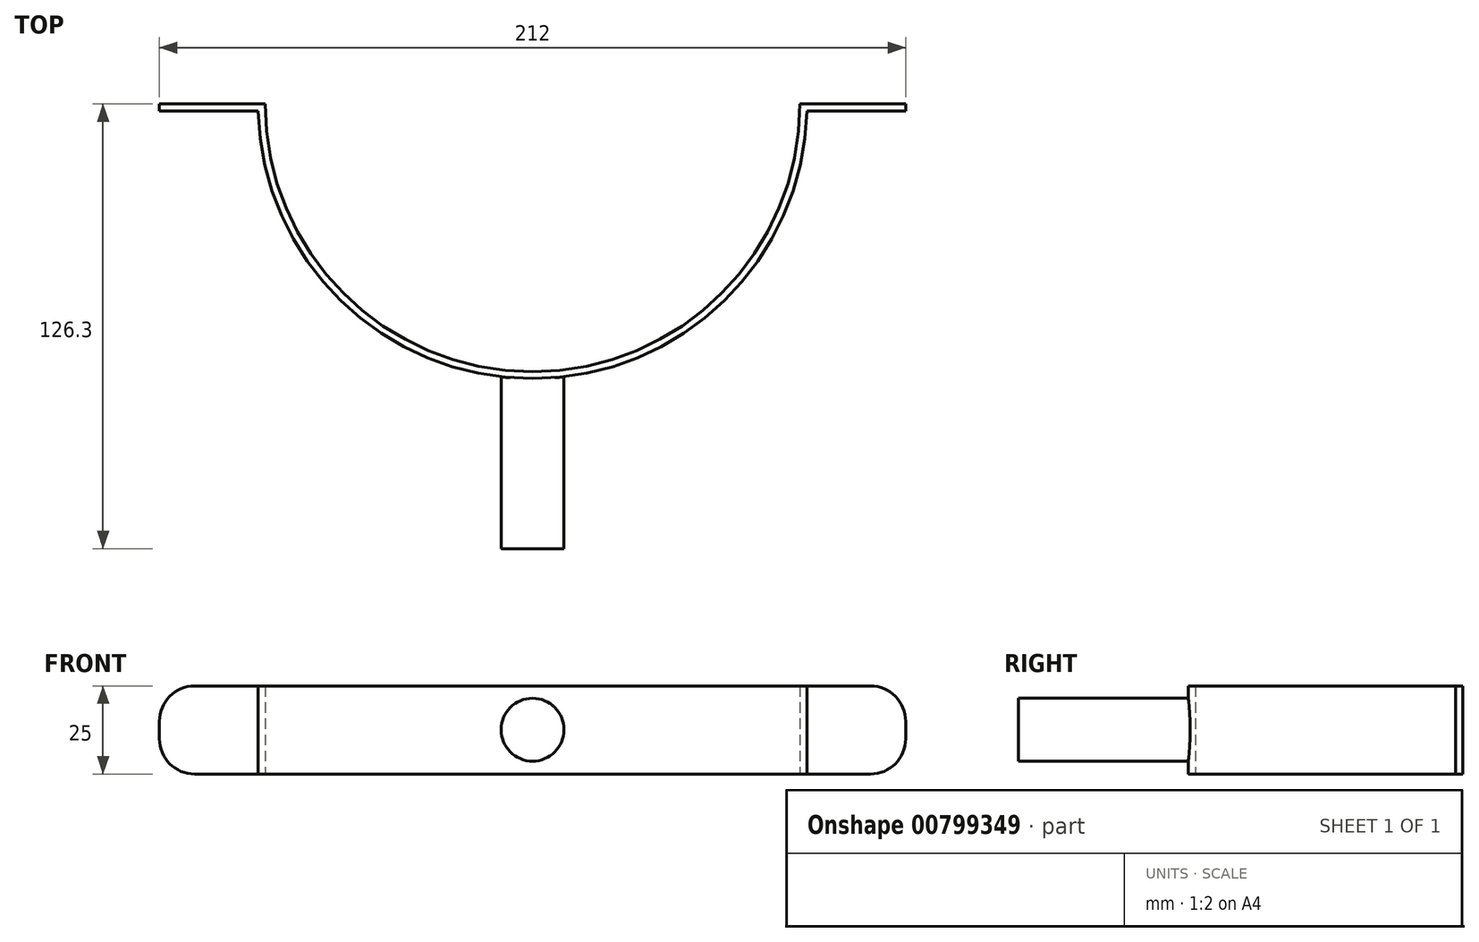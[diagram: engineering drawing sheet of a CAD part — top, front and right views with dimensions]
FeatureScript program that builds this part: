
annotation { "Feature Type Name" : "Feature", "Feature Type Description" : "" }
export const myFeature = defineFeature(function(context is Context, id is Id, definition is map)
    precondition{}
    {
        {
            var Q0;
            Q0=qCreatedBy(makeId("Top.planeOp"),FACE);
            var sketch = newSketch(context, id + "F0", { "sketchPlane" : qUnion([Q0])});
            skArc(sketch, "E0", {"start": v(-76, 0) * mm, "mid": v(0, -76) * mm, "end": v(76, 0) * mm});
            skLineSegment(sketch, "E1", {"start": v(-76, 0) * mm, "end": v(-106, 0) * mm});
            skLineSegment(sketch, "E2", {"start": v(-106, 0) * mm, "end": v(-76, 0) * mm});
            skLineSegment(sketch, "E3", {"start": v(76, 0) * mm, "end": v(106, 0) * mm});
            skArc(sketch, "E4", {"start": v(-77.97, -2) * mm, "mid": v(0, -78) * mm, "end": v(77.97, -2) * mm});
            skLineSegment(sketch, "E5", {"start": v(-106, 0) * mm, "end": v(-106, -2) * mm});
            skLineSegment(sketch, "E6", {"start": v(-106, -2) * mm, "end": v(-77.97, -2) * mm});
            skLineSegment(sketch, "E7", {"start": v(106, -2) * mm, "end": v(106, 0) * mm});
            skLineSegment(sketch, "E8.trimOffspring", {"start": v(77.97, -2) * mm, "end": v(106, -2) * mm});
            skSolve(sketch);
        }
        {
            var Q0;
            Q0=makeQuery(id+"F0.imprint","IMPRINT",FACE,{"disambiguationData":[TD([[makeQuery(id+"F0.imprint","IMPRINT",EDGE,{"derivedFrom":sQuery(id+"F0.wireOp",EDGE,"E0")}),-1.0]])]});
            extrude(context, id + "F1", {"entities" : qUnion([Q0]), "depth" : 25 * mm, "offsetDistance" : 25 * mm});
        }
        {
            var Q0;
            Q0=qCreatedBy(makeId("Front.planeOp"),FACE);
            cPlane(context, id + "F2", {"entities" : qUnion([Q0]), "cplaneType" : CPlaneType.OFFSET, "offset" : 76.3 * mm, "width" : 150 * mm, "height" : 150 * mm});
        }
        {
            var Q0;
            Q0=qCreatedBy(id+"F2.planeOp",FACE);
            var sketch = newSketch(context, id + "F3", { "sketchPlane" : qUnion([Q0])});
            skCircle(sketch, "E9", {"center": v(0, 12.6) * mm, "radius": 8.94 * mm});
            skSolve(sketch);
        }
        {
            var Q0;
            Q0 = qSketchRegion(id + "F3", true);
            extrude(context, id + "F4", {"entities" : qUnion([Q0]), "operationType" : NewBodyOperationType.ADD, "depth" : 50 * mm, "offsetDistance" : 25 * mm});
        }
        {
            var Q0;
            Q0=makeQuery(id+"F1.opExtrude","CAP_EDGE",EDGE,{"disambiguationData":[OSD([sQuery(id+"F0.wireOp",EDGE,"E7")])],"isStart":false});
            var Q1;
            Q1=makeQuery(id+"F1.opExtrude","CAP_EDGE",EDGE,{"disambiguationData":[OSD([sQuery(id+"F0.wireOp",EDGE,"E7")])],"isStart":true});
            var Q2;
            Q2=makeQuery(id+"F1.opExtrude","CAP_EDGE",EDGE,{"disambiguationData":[OSD([sQuery(id+"F0.wireOp",EDGE,"E5")])],"isStart":false});
            var Q3;
            Q3=makeQuery(id+"F1.opExtrude","CAP_EDGE",EDGE,{"disambiguationData":[OSD([sQuery(id+"F0.wireOp",EDGE,"E5")])],"isStart":true});
            fillet(context, id + "F5", {"entities" : qUnion([Q0, Q1, Q2, Q3]), "tangentPropagation" : true, "radius" : 10 * mm, "defaultsChanged" : false, "vertexSettings" : [], "allowEdgeOverflow" : false});
        }
    });
